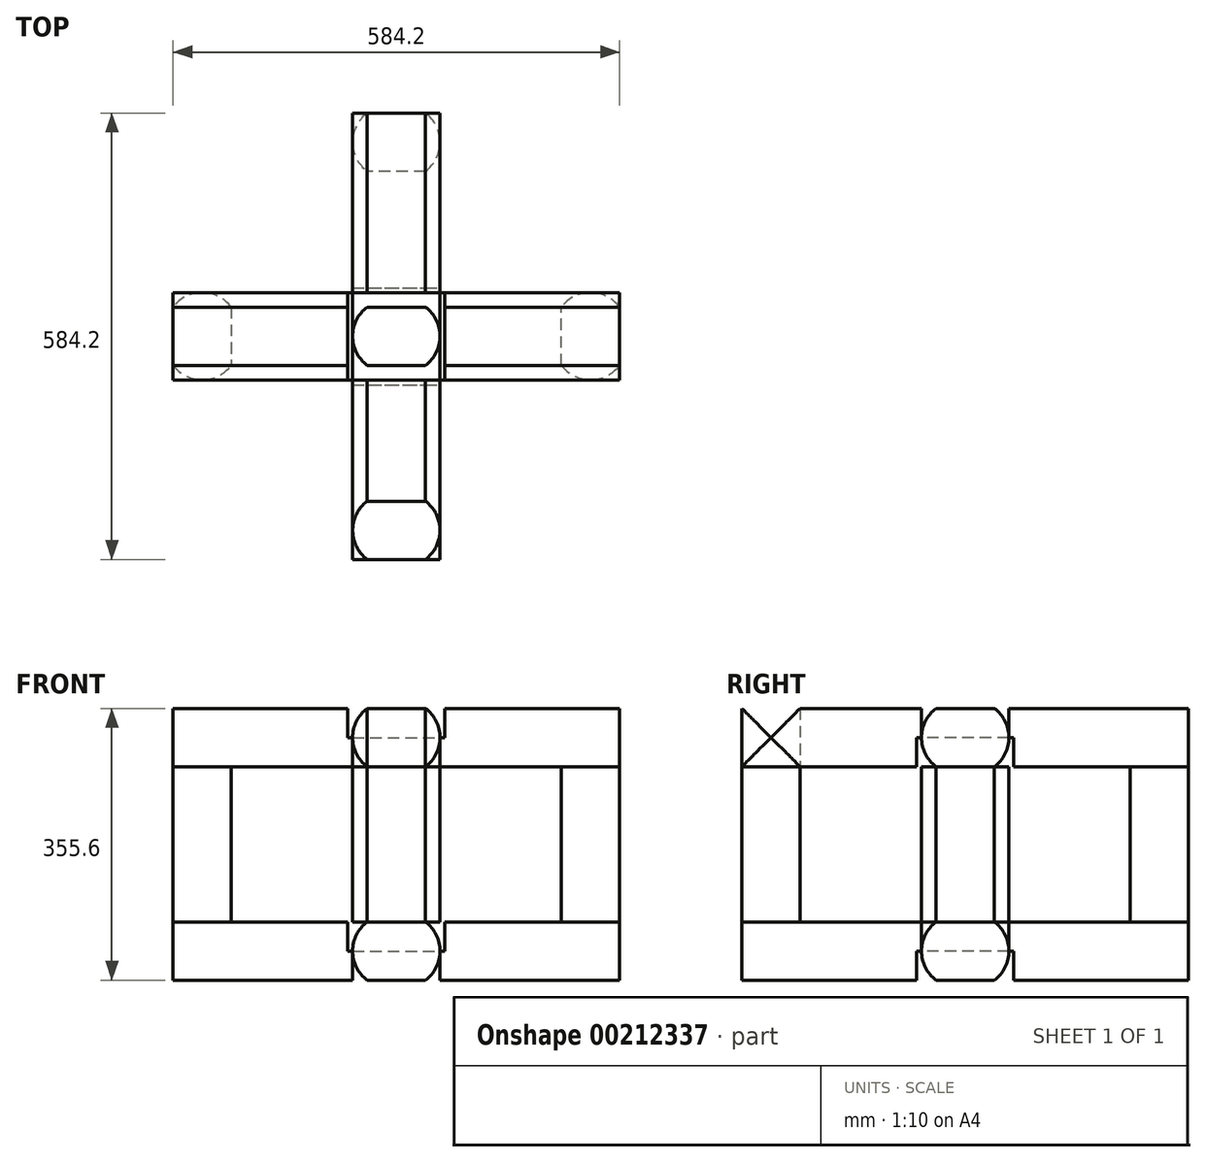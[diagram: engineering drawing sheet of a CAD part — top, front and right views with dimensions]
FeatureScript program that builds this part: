
annotation { "Feature Type Name" : "Feature", "Feature Type Description" : "" }
export const myFeature = defineFeature(function(context is Context, id is Id, definition is map)
    precondition{}
    {
        {
            var Q0;
            Q0=qCreatedBy(makeId("Front.planeOp"),FACE);
            var sketch = newSketch(context, id + "F0", { "sketchPlane" : qUnion([Q0])});
            skLineSegment(sketch, "E0", {"start": v(-38.1, 0) * mm, "end": v(38.1, 0) * mm});
            skLineSegment(sketch, "E1", {"start": v(-38.1, 76.2) * mm, "end": v(38.1, 76.2) * mm});
            skLineSegment(sketch, "E2", {"start": v(-38.1, 0) * mm, "end": v(-38.1, 76.2) * mm, "construction": true});
            skLineSegment(sketch, "E3", {"start": v(38.1, 0) * mm, "end": v(38.1, 76.2) * mm, "construction": true});
            skLineSegment(sketch, "E4.bottom", {"start": v(-57.15, 0) * mm, "end": v(57.15, 0) * mm, "construction": true});
            skLineSegment(sketch, "E4.top", {"start": v(-57.15, 76.2) * mm, "end": v(57.15, 76.2) * mm, "construction": true});
            skLineSegment(sketch, "E4.left", {"start": v(-57.15, 0) * mm, "end": v(-57.15, 76.2) * mm, "construction": true});
            skLineSegment(sketch, "E4.right", {"start": v(57.15, 0) * mm, "end": v(57.15, 76.2) * mm, "construction": true});
            skArc(sketch, "E5", {"start": v(-38.1, 76.2) * mm, "mid": v(-57.15, 38.1) * mm, "end": v(-38.1, 0) * mm});
            skArc(sketch, "E6", {"start": v(38.1, 0) * mm, "mid": v(57.15, 38.1) * mm, "end": v(38.1, 76.2) * mm});
            skLineSegment(sketch, "E7", {"start": v(0, 0) * mm, "end": v(0, 76.2) * mm, "construction": true});
            skSolve(sketch);
        }
        {
            var Q0;
            Q0=makeQuery(id+"F0.imprint","IMPRINT",FACE,{"disambiguationData":[TD([[makeQuery(id+"F0.imprint","IMPRINT",EDGE,{"derivedFrom":sQuery(id+"F0.wireOp",EDGE,"E0")}),1.0]])]});
            extrude(context, id + "F1", {"entities" : qUnion([Q0]), "depth" : 292.1 * mm, "hasSecondDirection" : true, "secondDirectionOppositeDirection" : true, "secondDirectionDepth" : 292.1 * mm});
        }
        {
            var Q0;
            Q0=makeQuery(id+"F1.opExtrude","SWEPT_BODY",BODY,{"disambiguationData":[OSD([sQuery(id+"F0.wireOp",EDGE,"E0"),sQuery(id+"F0.wireOp",EDGE,"E1"),sQuery(id+"F0.wireOp",EDGE,"E5"),sQuery(id+"F0.wireOp",EDGE,"E6")])]});
            var Q1;
            Q1=makeQuery(id+"F1.opExtrude","CAP_EDGE",EDGE,{"disambiguationData":[OSD([sQuery(id+"F0.wireOp",EDGE,"E1")])],"isStart":false});
            transform(context, id + "F2", {"entities" : qUnion([Q0]), "transformType" : TransformType.ROTATION, "transformAxis" : qUnion([Q1]), "angle" : 90 * degree, "makeCopy" : true});
        }
        {
            var Q0;
            Q0=makeQuery(id+"F1.opExtrude","SWEPT_BODY",BODY,{"disambiguationData":[OSD([sQuery(id+"F0.wireOp",EDGE,"E0"),sQuery(id+"F0.wireOp",EDGE,"E1"),sQuery(id+"F0.wireOp",EDGE,"E5"),sQuery(id+"F0.wireOp",EDGE,"E6")])]});
            var Q1;
            Q1=sQuery(id+"F0.wireOp",EDGE,"E7");
            transform(context, id + "F3", {"entities" : qUnion([Q0]), "transformType" : TransformType.ROTATION, "transformAxis" : qUnion([Q1]), "angle" : 90 * degree, "makeCopy" : true});
        }
        {
            var Q0;
            Q0=qCreatedBy(makeId("Right.planeOp"),FACE);
            var sketch = newSketch(context, id + "F4", { "sketchPlane" : qUnion([Q0])});
            skLineSegment(sketch, "E8.bottom", {"start": v(-57.15, 76.2) * mm, "end": v(57.15, 76.2) * mm});
            skLineSegment(sketch, "E8.top", {"start": v(-57.15, 38.1) * mm, "end": v(57.15, 38.1) * mm});
            skLineSegment(sketch, "E8.left", {"start": v(-57.15, 76.2) * mm, "end": v(-57.15, 38.1) * mm});
            skLineSegment(sketch, "E8.right", {"start": v(57.15, 76.2) * mm, "end": v(57.15, 38.1) * mm});
            skLineSegment(sketch, "E9", {"start": v(0, 0) * mm, "end": v(0, 38.1) * mm, "construction": true});
            skSolve(sketch);
        }
        {
            var Q0;
            Q0 = qSketchRegion(id + "F4", true);
            extrude(context, id + "F5", {"entities" : qUnion([Q0]), "operationType" : NewBodyOperationType.REMOVE, "oppositeDirection" : true, "depth" : 63.5 * mm, "hasSecondDirection" : true, "secondDirectionOppositeDirection" : false, "secondDirectionDepth" : 63.5 * mm});
        }
        {
            var Q0;
            Q0=qCreatedBy(makeId("Front.planeOp"),FACE);
            var sketch = newSketch(context, id + "F6", { "sketchPlane" : qUnion([Q0])});
            skLineSegment(sketch, "E10.bottom", {"start": v(-57.15, 38.1) * mm, "end": v(57.15, 38.1) * mm});
            skLineSegment(sketch, "E10.top", {"start": v(-57.15, 0) * mm, "end": v(57.15, 0) * mm});
            skLineSegment(sketch, "E10.left", {"start": v(-57.15, 38.1) * mm, "end": v(-57.15, 0) * mm});
            skLineSegment(sketch, "E10.right", {"start": v(57.15, 38.1) * mm, "end": v(57.15, 0) * mm});
            skSolve(sketch);
        }
        {
            var Q0;
            Q0 = qSketchRegion(id + "F6", true);
            extrude(context, id + "F7", {"entities" : qUnion([Q0]), "operationType" : NewBodyOperationType.REMOVE, "oppositeDirection" : true, "depth" : 63.5 * mm, "hasSecondDirection" : true, "secondDirectionOppositeDirection" : false, "secondDirectionDepth" : 63.5 * mm});
        }
        {
            var Q0;
            Q0=makeQuery(id+"F1.opExtrude","SWEPT_BODY",BODY,{"disambiguationData":[OSD([sQuery(id+"F0.wireOp",EDGE,"E0"),sQuery(id+"F0.wireOp",EDGE,"E1"),sQuery(id+"F0.wireOp",EDGE,"E5"),sQuery(id+"F0.wireOp",EDGE,"E6")])]});
            var Q1;
            Q1=makeQuery(id+"F3.opPattern","COPY",BODY,{"derivedFrom":makeQuery(id+"F1.opExtrude","SWEPT_BODY",BODY,{"disambiguationData":[OSD([sQuery(id+"F0.wireOp",EDGE,"E0"),sQuery(id+"F0.wireOp",EDGE,"E1"),sQuery(id+"F0.wireOp",EDGE,"E5"),sQuery(id+"F0.wireOp",EDGE,"E6")])]}),"instanceName":"1"});
            transform(context, id + "F8", {"entities" : qUnion([Q0, Q1]), "transformType" : TransformType.TRANSLATION_3D, "dx" : 0 * mm, "dy" : 0 * mm, "dz" : 279.4 * mm, "makeCopy" : true});
        }
        {
            var Q0;
            Q0=makeQuery(id+"F8.opPattern","COPY",FACE,{"derivedFrom":makeQuery(id+"F1.opExtrude","SWEPT_FACE",FACE,{"disambiguationData":[OSD([sQuery(id+"F0.wireOp",EDGE,"E0")])]}),"instanceName":"1"});
            var sketch = newSketch(context, id + "F9", { "sketchPlane" : qUnion([Q0])});
            skLineSegment(sketch, "E11.0.0", {"start": v(38.1, 292.1) * mm, "end": v(-38.1, 292.1) * mm});
            skArc(sketch, "E11.0.1", {"start": v(-38.1, 292.1) * mm, "mid": v(-57.15, 254) * mm, "end": v(-38.1, 215.9) * mm});
            skLineSegment(sketch, "E11.0.2", {"start": v(-38.1, 215.9) * mm, "end": v(38.1, 215.9) * mm});
            skArc(sketch, "E11.0.3", {"start": v(38.1, 215.9) * mm, "mid": v(57.15, 254) * mm, "end": v(38.1, 292.1) * mm});
            skSolve(sketch);
        }
        {
            var Q0;
            Q0 = qSketchRegion(id + "F9", true);
            extrude(context, id + "F10", {"entities" : qUnion([Q0]), "operationType" : NewBodyOperationType.REMOVE, "oppositeDirection" : true, "depth" : 762 * mm});
        }
        {
            var Q0;
            Q0=makeQuery(id+"F2.opPattern","COPY",BODY,{"derivedFrom":makeQuery(id+"F1.opExtrude","SWEPT_BODY",BODY,{"disambiguationData":[OSD([sQuery(id+"F0.wireOp",EDGE,"E0"),sQuery(id+"F0.wireOp",EDGE,"E1"),sQuery(id+"F0.wireOp",EDGE,"E5"),sQuery(id+"F0.wireOp",EDGE,"E6")])]}),"instanceName":"1"});
            var Q1;
            Q1=sQuery(id+"F0.wireOp",EDGE,"E7");
            circularPattern(context, id + "F11", {"entities" : qUnion([Q0]), "axis" : qUnion([Q1]), "angle" : 360 * degree, "instanceCount" : 4, "equalSpace" : true});
        }
        {
            var Q0;
            Q0=makeQuery(id+"F2.opPattern","COPY",BODY,{"derivedFrom":makeQuery(id+"F1.opExtrude","SWEPT_BODY",BODY,{"disambiguationData":[OSD([sQuery(id+"F0.wireOp",EDGE,"E0"),sQuery(id+"F0.wireOp",EDGE,"E1"),sQuery(id+"F0.wireOp",EDGE,"E5"),sQuery(id+"F0.wireOp",EDGE,"E6")])]}),"instanceName":"1"});
            transform(context, id + "F12", {"entities" : qUnion([Q0]), "transformType" : TransformType.TRANSLATION_3D, "dx" : 0 * mm, "dy" : 254 * mm, "dz" : 0 * mm, "makeCopy" : true});
        }
    });
